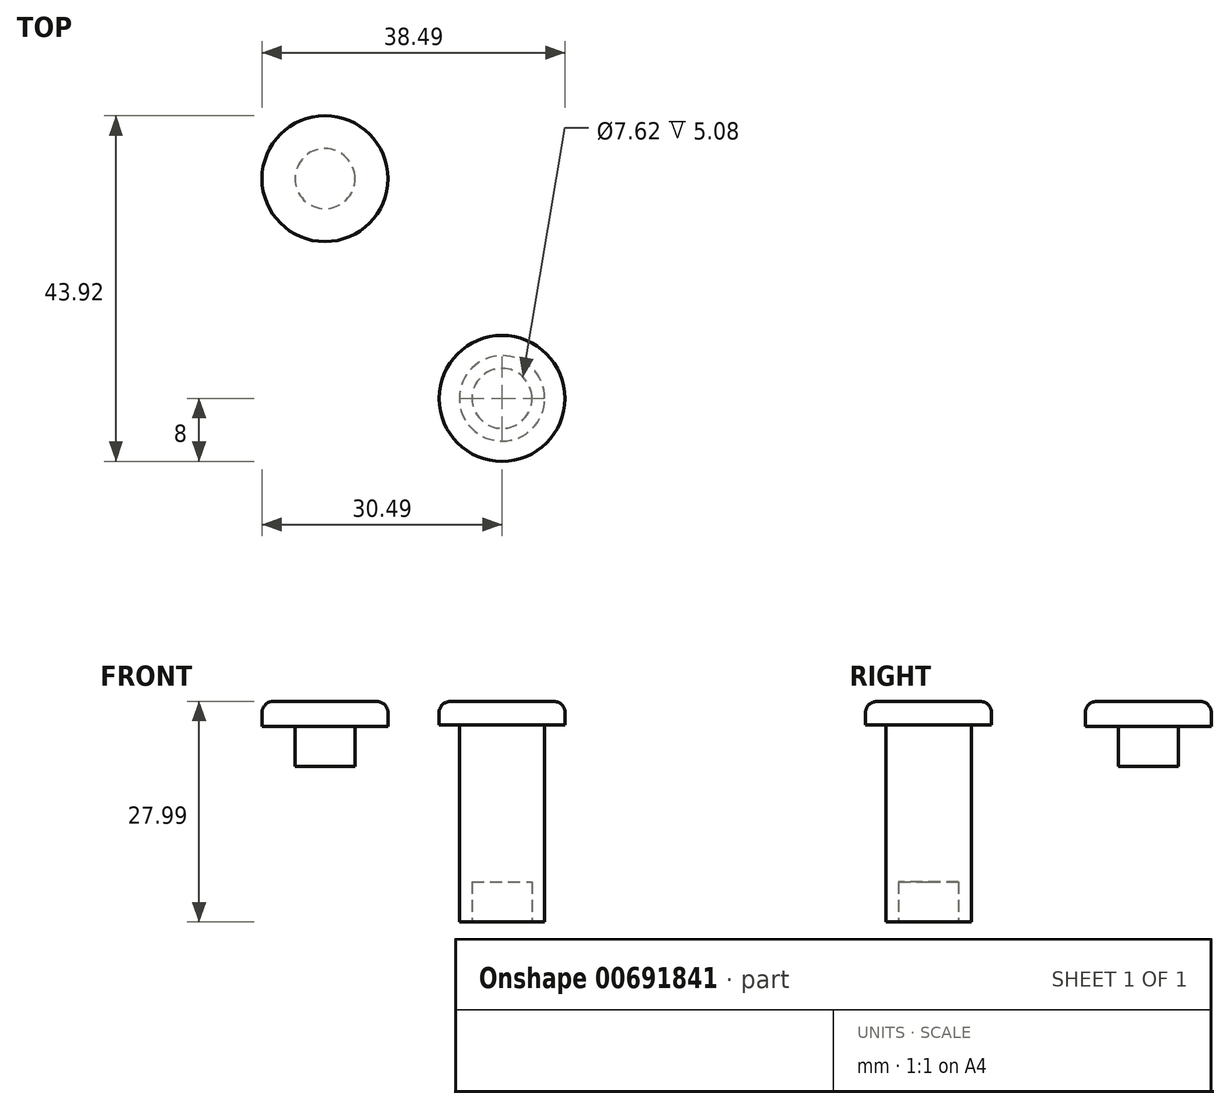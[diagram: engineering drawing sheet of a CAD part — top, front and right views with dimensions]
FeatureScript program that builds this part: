
annotation { "Feature Type Name" : "Feature", "Feature Type Description" : "" }
export const myFeature = defineFeature(function(context is Context, id is Id, definition is map)
    precondition{}
    {
        {
            var Q0;
            Q0=qCreatedBy(makeId("Top.planeOp"),FACE);
            var sketch = newSketch(context, id + "F0", { "sketchPlane" : qUnion([Q0])});
            skCircle(sketch, "E0", {"center": v(0, 0) * mm, "radius": 5.42 * mm});
            skSolve(sketch);
        }
        {
            var Q0;
            Q0 = qSketchRegion(id + "F0", true);
            extrude(context, id + "F1", {"entities" : qUnion([Q0]), "depth" : 25 * mm, "offsetDistance" : 25.4 * mm});
        }
        {
            var Q0;
            Q0=makeQuery(id+"F1.opExtrude","CAP_FACE",FACE,{"disambiguationData":[OSD([sQuery(id+"F0.wireOp",EDGE,"E0")])],"isStart":false});
            var sketch = newSketch(context, id + "F2", { "sketchPlane" : qUnion([Q0])});
            skCircle(sketch, "E1", {"center": v(0, 0) * mm, "radius": 8 * mm});
            skSolve(sketch);
        }
        {
            var Q0;
            Q0 = qSketchRegion(id + "F2", true);
            extrude(context, id + "F3", {"entities" : qUnion([Q0]), "operationType" : NewBodyOperationType.ADD, "depth" : 3 * mm, "offsetDistance" : 25.4 * mm});
        }
        {
            var Q0;
            Q0=makeQuery(id+"F3.opExtrude","CAP_EDGE",EDGE,{"disambiguationData":[OSD([sQuery(id+"F2.wireOp",EDGE,"E1")])],"isStart":false});
            fillet(context, id + "F4", {"entities" : qUnion([Q0]), "radius" : 1.42 * mm, "tangentPropagation" : true, "allowEdgeOverflow" : false});
        }
        {
            var Q0;
            Q0=qCreatedBy(makeId("Top.planeOp"),FACE);
            cPlane(context, id + "F5", {"entities" : qUnion([Q0]), "cplaneType" : CPlaneType.OFFSET, "offset" : 28 * mm, "width" : 152.4 * mm, "height" : 152.4 * mm});
        }
        {
            var Q0;
            Q0=makeQuery(id+"F1.opExtrude","CAP_FACE",FACE,{"disambiguationData":[OSD([sQuery(id+"F0.wireOp",EDGE,"E0")])],"isStart":true});
            var sketch = newSketch(context, id + "F6", { "sketchPlane" : qUnion([Q0])});
            skCircle(sketch, "E2", {"center": v(0, 0) * mm, "radius": 3.81 * mm});
            skSolve(sketch);
        }
        {
            var Q0;
            Q0 = qSketchRegion(id + "F6", true);
            extrude(context, id + "F7", {"entities" : qUnion([Q0]), "operationType" : NewBodyOperationType.REMOVE, "oppositeDirection" : true, "depth" : 5.08 * mm, "offsetDistance" : 25.4 * mm});
        }
        {
            var Q0;
            Q0=qCreatedBy(id+"F5.planeOp",FACE);
            var sketch = newSketch(context, id + "F8", { "sketchPlane" : qUnion([Q0])});
            skCircle(sketch, "E3", {"center": v(-22.49, 27.92) * mm, "radius": 8 * mm});
            skSolve(sketch);
        }
        {
            var Q0;
            Q0 = qSketchRegion(id + "F8", true);
            extrude(context, id + "F9", {"entities" : qUnion([Q0]), "oppositeDirection" : true, "depth" : 3.15 * mm, "offsetDistance" : 25.4 * mm});
        }
        {
            var Q0;
            Q0=makeQuery(id+"F9.opExtrude","CAP_FACE",FACE,{"disambiguationData":[OSD([sQuery(id+"F8.wireOp",EDGE,"E3")])],"isStart":false});
            var sketch = newSketch(context, id + "F10", { "sketchPlane" : qUnion([Q0])});
            skCircle(sketch, "E4", {"center": v(-22.49, -27.92) * mm, "radius": 3.81 * mm});
            skSolve(sketch);
        }
        {
            var Q0;
            Q0 = qSketchRegion(id + "F10", true);
            extrude(context, id + "F11", {"entities" : qUnion([Q0]), "operationType" : NewBodyOperationType.ADD, "depth" : 5.08 * mm, "offsetDistance" : 25.4 * mm});
        }
        {
            var Q0;
            Q0=makeQuery(id+"F9.opExtrude","CAP_EDGE",EDGE,{"disambiguationData":[OSD([sQuery(id+"F8.wireOp",EDGE,"E3")])],"isStart":true});
            fillet(context, id + "F12", {"entities" : qUnion([Q0]), "radius" : 1.42 * mm, "tangentPropagation" : true, "allowEdgeOverflow" : false});
        }
    });
